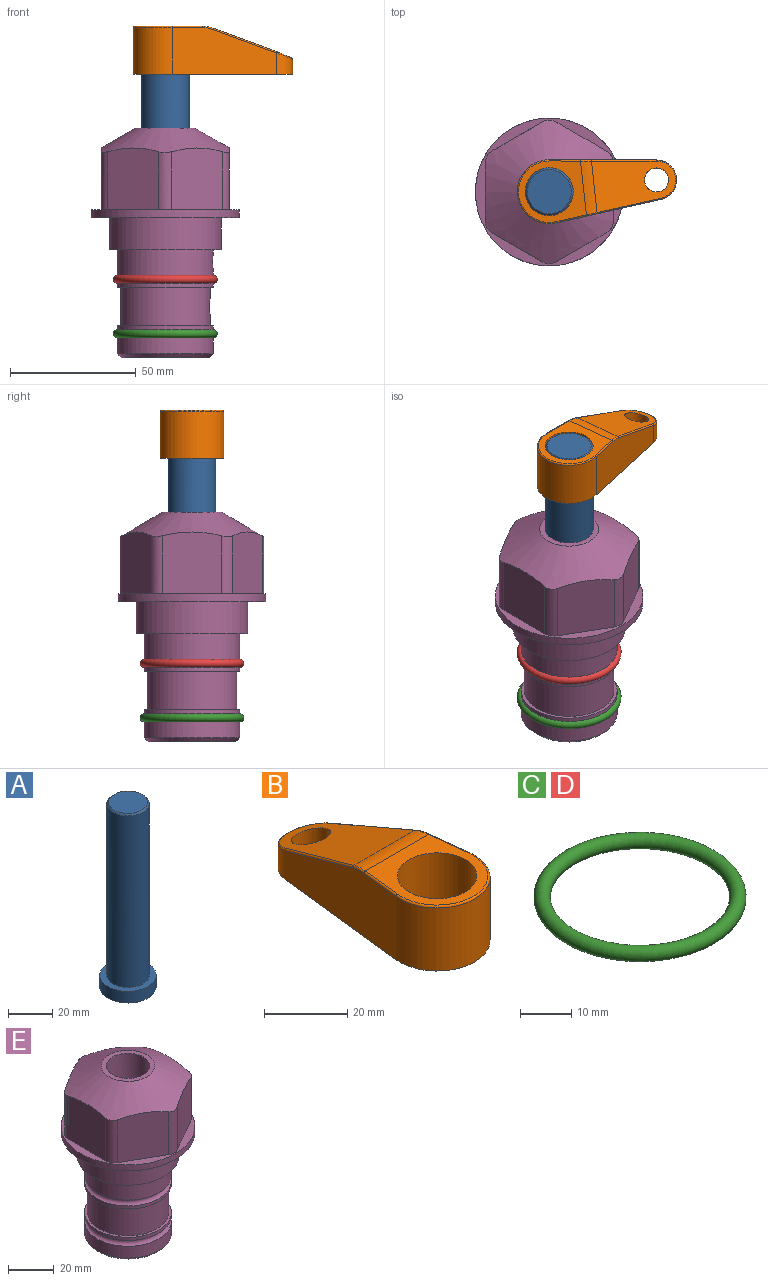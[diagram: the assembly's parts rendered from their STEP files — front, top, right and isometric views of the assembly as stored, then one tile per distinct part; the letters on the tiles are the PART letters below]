
ASSEMBLY  parts=5 mates=3
PART A: 6 faces, bbox 25.4x25.4x101.6 mm
  f0: plane 17.46x17.46mm, normal (0,0,1), area 239.5mm2, adj f5
  f1: plane 25.4x25.4mm, normal (0,0,-1), area 506.7mm2, adj f2
  f2: cylinder r=12.7mm len=25.4mm, axis (0,0,1), area 506.7mm2, adj f1,f3
  f3: plane 25.4x25.4mm, normal (0,0,1), area 221.7mm2, adj f2,f4
  f4: cylinder r=9.53mm len=94.46mm, axis (0,0,1), area 5653mm2, adj f3,f5
  f5: cone r=8.73mm half-angle=45deg, axis (0,0,-1), area 64.4mm2, adj f0,f4
PART B: 44 faces, bbox 27.5x64.5x19.1 mm
  f0: plane 2.3x0.95mm, normal (0,0,-1), area 1mm2, adj f25,f30,f34
  f1: plane 63.5x25.4mm, normal (0,0,-1), area 561.7mm2, adj f2,f3,f4,f5,f6,f7,f19,f20
  f2: cylinder r=12.7mm len=25.4mm, axis (0,0,-1), area 792.2mm2, adj f1,f3,f5,f13
  f3: plane 42.33x18.54mm, normal (0.99,0.11,0), area 647mm2, adj f1,f2,f4,f11,f12,f14
  f4: cylinder r=7.94mm len=15.78mm, axis (0,0,-1), area 158.6mm2, adj f1,f3,f5,f16
  f5: plane 42.33x18.54mm, normal (-0.99,0.11,0), area 647mm2, adj f1,f2,f4,f15,f17,f18
  f6: cylinder r=9.53mm len=19.05mm, axis (0,0,-1), area 1140.1mm2, adj f1,f8
  f7: cylinder r=4.76mm len=10.98mm, axis (0,0,-1), area 276.1mm2, adj f1,f9
  f8: plane 25.83x24.38mm, normal (0,0,1), area 262.2mm2, adj f6,f10,f11,f13,f15
  f9: plane 32.49x20.55mm, normal (0,0.34,0.94), area 489.9mm2, adj f7,f10,f14,f16,f18
  f10: cylinder r=12.7mm len=21.49mm, axis (-1,0,0), area 93.2mm2, adj f8,f9,f12,f17
  f11: cylinder r=0.51mm len=12.34mm, axis (0.11,-0.99,0), area 9.9mm2, adj f3,f8,f12,f13
  f12: bspline ~7.62x1.64mm, area 3.5mm2, adj f3,f10,f11,f14
  f13: torus R=12.19mm, axis (0,0,1), area 33.6mm2, adj f2,f8,f11,f15
  f14: cylinder r=0.51mm len=26.01mm, axis (0.1,-0.93,0.34), area 21.6mm2, adj f3,f9,f12,f16
  f15: cylinder r=0.51mm len=12.34mm, axis (0.11,0.99,0), area 9.9mm2, adj f5,f8,f13,f17
  f16: bspline ~15.78x7.05mm, area 15.7mm2, adj f4,f9,f14,f18
  f17: bspline ~7.62x1.64mm, area 3.5mm2, adj f5,f10,f15,f18
  f18: cylinder r=0.51mm len=26.01mm, axis (0.1,0.93,-0.34), area 21.6mm2, adj f5,f9,f16,f17
  f19: plane 21.6x14.29mm, normal (-0.99,-0.11,0), area 242.6mm2, adj f1,f26,f28,f34,f36,f38
  f20: plane 21.6x14.29mm, normal (0.99,-0.11,0), area 242.6mm2, adj f1,f27,f29,f37,f39,f41
  f21: cylinder r=12.7mm len=14.29mm, axis (0,0,-1), area 173.2mm2, adj f1,f26,f27,f30,f31,f33
  f22: cylinder r=7.94mm len=7.63mm, axis (0,0,-1), area 53.8mm2, adj f1,f28,f29,f42
  f23: plane 2.3x0.95mm, normal (0,0,-1), area 1mm2, adj f25,f33,f37
  f24: plane 17.94x12.32mm, normal (0,-0.34,-0.94), area 191.2mm2, adj f25,f38,f41,f42
  f25: cylinder r=9.53mm len=12.93mm, axis (-1,0,0), area 37.5mm2, adj f0,f23,f24,f31,f36,f39
  f26: cylinder r=1.59mm len=14.29mm, axis (0,0,-1), area 49mm2, adj f1,f19,f21,f32
  f27: cylinder r=1.59mm len=14.29mm, axis (0,0,-1), area 49mm2, adj f1,f20,f21,f35
  f28: cylinder r=1.59mm len=7.28mm, axis (0,0,-1), area 22.1mm2, adj f1,f19,f22,f40
  f29: cylinder r=1.59mm len=7.28mm, axis (0,0,-1), area 22.1mm2, adj f1,f20,f22,f43
  f30: torus R=14.29mm, axis (0,0,1), area 5.8mm2, adj f0,f21,f31,f32
  f31: bspline ~11.06x2.73mm, area 20.8mm2, adj f21,f25,f30,f33
  f32: sphere r=1.59mm, area 5.4mm2, adj f26,f30,f34
  f33: torus R=14.29mm, axis (0,0,1), area 5.8mm2, adj f21,f23,f31,f35
  f34: cylinder r=1.59mm len=1.68mm, axis (-0.11,0.99,0), area 2.4mm2, adj f0,f19,f32,f36
  f35: sphere r=1.59mm, area 5.4mm2, adj f27,f33,f37
  f36: bspline ~5.82x2.33mm, area 7.7mm2, adj f19,f25,f34,f38
  f37: cylinder r=1.59mm len=1.68mm, axis (0.11,0.99,0), area 2.4mm2, adj f20,f23,f35,f39
  f38: cylinder r=1.59mm len=18.33mm, axis (0.1,-0.93,0.34), area 46.7mm2, adj f19,f24,f36,f40
  f39: bspline ~5.82x2.33mm, area 7.7mm2, adj f20,f25,f37,f41
  f40: sphere r=1.59mm, area 3.6mm2, adj f28,f38,f42
  f41: cylinder r=1.59mm len=18.33mm, axis (0.1,0.93,-0.34), area 46.7mm2, adj f20,f24,f39,f43
  f42: bspline ~8.31x1.84mm, area 15.3mm2, adj f22,f24,f40,f43
  f43: sphere r=1.59mm, area 3.6mm2, adj f29,f41,f42
PART C: 1 faces, bbox 44.7x44.7x3.2 mm
  f0: torus R=19.05mm, axis (0,0,1), area 1193.9mm2
PART D: same geometry as C
PART E: 36 faces, bbox 58.7x58.7x91.2 mm
  f0: cylinder r=17.78mm len=35.56mm, axis (0,0,1), area 1670.8mm2, adj f23,f24,f31
  f1: cylinder r=19.05mm len=38.1mm, axis (0,0,1), area 1191.9mm2, adj f26,f27,f30
  f2: plane 58.66x58.66mm, normal (0,0,-1), area 1150.6mm2, adj f3,f28
  f3: cylinder r=29.33mm len=58.66mm, axis (0,0,-1), area 585.1mm2, adj f2,f4
  f4: plane 58.66x58.66mm, normal (0,0,1), area 475.9mm2, adj f3,f5,f6,f7,f8,f9,f10,f11
  f5: plane 24.5x20.32mm, normal (-0.5,0.87,0), area 562.8mm2, adj f4,f15,f16,f17
  f6: plane 24.5x20.32mm, normal (0.5,0.87,0), area 562.8mm2, adj f4,f14,f15,f17
  f7: plane 24.5x23.48mm, normal (1,0,0), area 562.8mm2, adj f4,f13,f14,f17
  f8: plane 24.5x20.32mm, normal (0.5,-0.87,0), area 562.8mm2, adj f4,f12,f13,f17
  f9: plane 24.5x20.32mm, normal (-0.5,-0.87,0), area 562.8mm2, adj f4,f11,f12,f17
  f10: plane 24.5x23.48mm, normal (-1,0,0), area 562.8mm2, adj f4,f11,f16,f17
  f11: cylinder r=5.08mm len=23.01mm, axis (0,0,-1), area 121.2mm2, adj f4,f9,f10,f17
  f12: cylinder r=5.08mm len=23.01mm, axis (0,0,-1), area 121.2mm2, adj f4,f8,f9,f17
  f13: cylinder r=5.08mm len=23.01mm, axis (0,0,-1), area 121.2mm2, adj f4,f7,f8,f17
  f14: cylinder r=5.08mm len=23.01mm, axis (0,0,-1), area 121.2mm2, adj f4,f6,f7,f17
  f15: cylinder r=5.08mm len=23.01mm, axis (0,0,-1), area 121.2mm2, adj f4,f5,f6,f17
  f16: cylinder r=5.08mm len=23.01mm, axis (0,0,-1), area 121.2mm2, adj f4,f5,f10,f17
  f17: cone r=11.73mm half-angle=60deg, axis (0,0,-1), area 2071.8mm2, adj f5,f6,f7,f8,f9,f10,f11,f12
  f18: plane 23.46x23.46mm, normal (0,0,1), area 147.4mm2, adj f17,f35
  f19: plane 34.93x34.93mm, normal (0,0,-1), area 958mm2, adj f29
  f20: cylinder r=19.05mm len=38.1mm, axis (0,0,1), area 760.1mm2, adj f21,f29
  f21: torus R=19.05mm, axis (0,0,1), area 565.3mm2, adj f20,f22
  f22: cylinder r=19.05mm len=38.1mm, axis (0,0,1), area 190mm2, adj f21,f23
  f23: plane 38.1x38.1mm, normal (0,0,1), area 146.9mm2, adj f0,f22
  f24: plane 38.1x38.1mm, normal (0,0,-1), area 146.9mm2, adj f0,f25
  f25: cylinder r=19.05mm len=38.1mm, axis (0,0,1), area 190mm2, adj f24,f26
  f26: torus R=19.05mm, axis (0,0,1), area 565.3mm2, adj f1,f25
  f27: plane 44.45x44.45mm, normal (0,0,-1), area 411.7mm2, adj f1,f28
  f28: cylinder r=22.23mm len=44.45mm, axis (0,0,1), area 1773.5mm2, adj f2,f27
  f29: cone r=19.05mm half-angle=45deg, axis (0,0,1), area 257.5mm2, adj f19,f20
  f30: cylinder r=3.17mm len=6.75mm, axis (-1,0,0), area 128mm2, adj f1,f33
  f31: cylinder r=3.17mm len=6.35mm, axis (-1,0,0), area 102.5mm2, adj f0,f33
  f32: plane 25.4x25.4mm, normal (0,0,1), area 506.7mm2, adj f33
  f33: cylinder r=12.7mm len=66.42mm, axis (0,0,-1), area 5236.2mm2, adj f30,f31,f32,f34
  f34: cone r=9.53mm half-angle=30deg, axis (0,0,-1), area 443.4mm2, adj f33,f35
  f35: cylinder r=9.53mm len=19.05mm, axis (0,0,-1), area 849mm2, adj f18,f34
PLACE A rot(axis=(0,0,1),6.2deg) t=(0,0,2.34)mm
PLACE B rot(axis=(0,0,-1),83.8deg) t=(0,0,56.95)mm
PLACE C t=(0,0,-21.59)mm
PLACE D at identity
PLACE E at identity fixed
MATE fastened C.f0 <-> E.f0  axis (0,0,1) through (0,0,-46.1)mm
MATE cylindrical A.f2 <-> E.f0  axis (0,0,1) through (0,0,27.98)mm
MATE fastened B.f2 <-> A.f2  axis (0,0,1) through (0,0,76)mm
